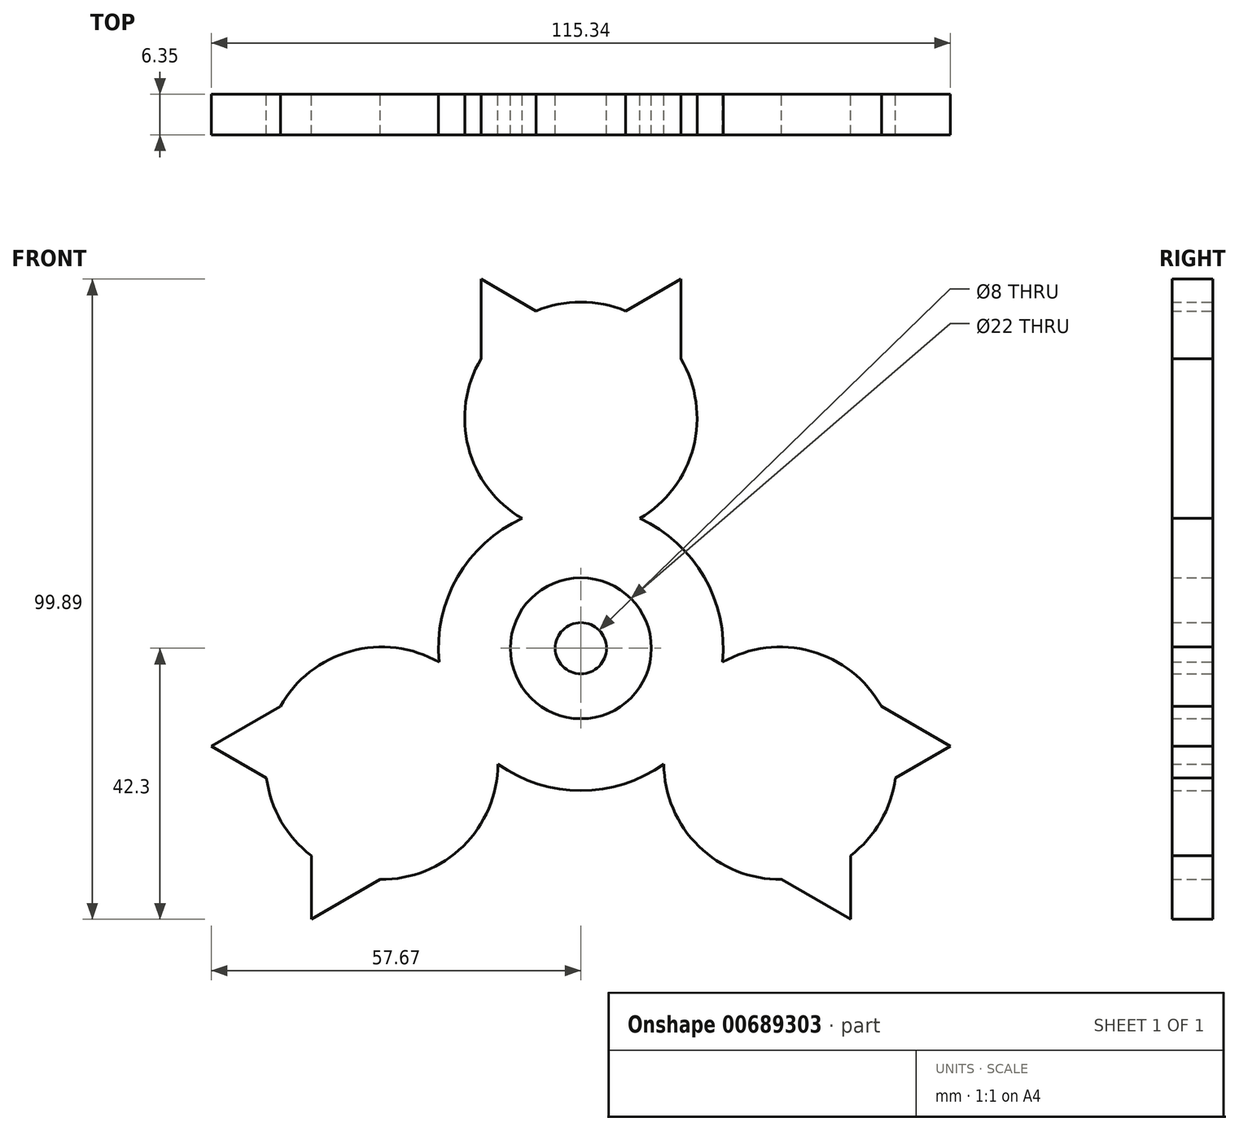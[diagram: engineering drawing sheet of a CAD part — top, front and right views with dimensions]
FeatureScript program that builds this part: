
annotation { "Feature Type Name" : "Feature", "Feature Type Description" : "" }
export const myFeature = defineFeature(function(context is Context, id is Id, definition is map)
    precondition{}
    {
        {
            var Q0;
            Q0=qCreatedBy(makeId("Front.planeOp"),FACE);
            var sketch = newSketch(context, id + "F0", { "sketchPlane" : qUnion([Q0])});
            skCircle(sketch, "E0", {"center": v(0, 0) * mm, "radius": 63.5 * mm, "construction": true});
            skArc(sketch, "E1", {"start": v(-9.18, 20.24) * mm, "mid": v(-19.25, 11.11) * mm, "end": v(-22.12, -2.17) * mm});
            skArc(sketch, "E2", {"start": v(9.18, 20.24) * mm, "mid": v(0, 54.02) * mm, "end": v(-9.18, 20.24) * mm});
            skCircle(sketch, "E3", {"center": v(0, 0) * mm, "radius": 11 * mm});
            skCircle(sketch, "E4", {"center": v(0, 0) * mm, "radius": 4 * mm});
            skLineSegment(sketch, "E5", {"start": v(-15.6, 45.14) * mm, "end": v(-15.6, 57.59) * mm});
            skLineSegment(sketch, "E6", {"start": v(-15.6, 57.59) * mm, "end": v(-6.99, 52.62) * mm});
            skPoint(sketch, "E7.0.midPoint", {"position": v(11, 35.88) * mm});
            skLineSegment(sketch, "E8.MirrorCS", {"start": v(15.6, 45.14) * mm, "end": v(15.6, 57.59) * mm});
            skLineSegment(sketch, "E9.MirrorCS", {"start": v(15.6, 57.59) * mm, "end": v(6.99, 52.62) * mm});
            skLineSegment(sketch, "E10.1.8", {"start": v(12.94, -18.07) * mm, "end": v(12.94, -18.07) * mm});
            skLineSegment(sketch, "E11", {"start": v(0, 35.88) * mm, "end": v(0, 0) * mm, "construction": true});
            skLineSegment(sketch, "E12", {"start": v(0, 0) * mm, "end": v(31.08, -17.94) * mm, "construction": true});
            skArc(sketch, "E13.trimOffspring", {"start": v(22.12, -2.17) * mm, "mid": v(19.25, 11.11) * mm, "end": v(9.18, 20.24) * mm});
            skLineSegment(sketch, "E14", {"start": v(0, 0) * mm, "end": v(-31.08, -17.94) * mm, "construction": true});
            skArc(sketch, "E15.1.0", {"start": v(-22.12, -2.17) * mm, "mid": v(-46.78, -27) * mm, "end": v(-12.94, -18.07) * mm});
            skLineSegment(sketch, "E15.1.1", {"start": v(-31.3, -36.07) * mm, "end": v(-42.08, -42.3) * mm});
            skLineSegment(sketch, "E15.1.2", {"start": v(-42.08, -42.3) * mm, "end": v(-42.08, -32.36) * mm});
            skLineSegment(sketch, "E15.1.3", {"start": v(-57.67, -15.29) * mm, "end": v(-49.06, -20.26) * mm});
            skLineSegment(sketch, "E15.1.4", {"start": v(-46.89, -9.07) * mm, "end": v(-57.67, -15.29) * mm});
            skArc(sketch, "E15.2.0", {"start": v(12.94, -18.07) * mm, "mid": v(46.78, -27) * mm, "end": v(22.12, -2.17) * mm});
            skLineSegment(sketch, "E15.2.1", {"start": v(46.89, -9.07) * mm, "end": v(57.67, -15.29) * mm});
            skLineSegment(sketch, "E15.2.2", {"start": v(57.67, -15.29) * mm, "end": v(49.06, -20.26) * mm});
            skLineSegment(sketch, "E15.2.3", {"start": v(42.08, -42.3) * mm, "end": v(42.08, -32.36) * mm});
            skLineSegment(sketch, "E15.2.4", {"start": v(31.3, -36.07) * mm, "end": v(42.08, -42.3) * mm});
            skArc(sketch, "E16.trimOffspring", {"start": v(-12.94, -18.07) * mm, "mid": v(0, -22.22) * mm, "end": v(12.94, -18.07) * mm});
            skSolve(sketch);
        }
        {
            var Q0;
            Q0 = qSketchRegion(id + "F0", true);
            extrude(context, id + "F1", {"entities" : qUnion([Q0]), "depth" : 6.35 * mm, "offsetDistance" : 25.4 * mm});
        }
        {
            var Q0;
            Q0=makeQuery(id+"F0.imprint","IMPRINT",FACE,{"disambiguationData":[TD([[makeQuery(id+"F0.imprint","IMPRINT",EDGE,{"derivedFrom":sQuery(id+"F0.wireOp",EDGE,"E3")}),1.0]])]});
            extrude(context, id + "F2", {"entities" : qUnion([Q0]), "depth" : 6.35 * mm, "offsetDistance" : 25.4 * mm});
        }
    });
